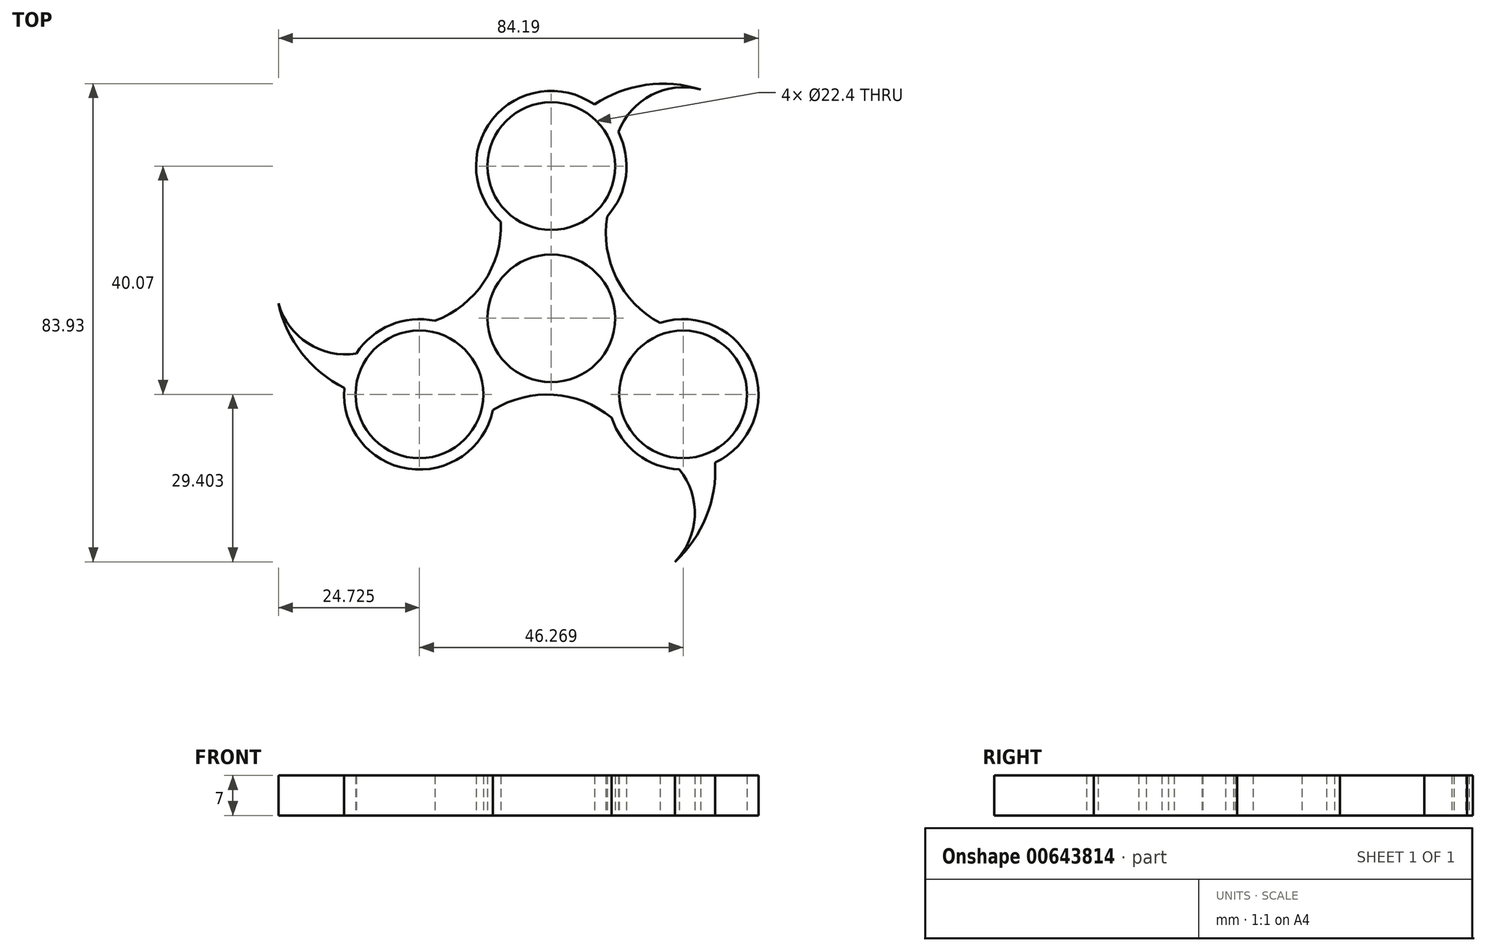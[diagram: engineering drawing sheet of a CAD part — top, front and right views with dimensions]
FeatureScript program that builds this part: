
annotation { "Feature Type Name" : "Feature", "Feature Type Description" : "" }
export const myFeature = defineFeature(function(context is Context, id is Id, definition is map)
    precondition{}
    {
        {
            var Q0;
            Q0=qCreatedBy(makeId("Top.planeOp"),FACE);
            var sketch = newSketch(context, id + "F0", { "sketchPlane" : qUnion([Q0])});
            skCircle(sketch, "E0", {"center": v(0, 0) * mm, "radius": 11.2 * mm});
            skCircle(sketch, "E1", {"center": v(0, 26.71) * mm, "radius": 11.2 * mm});
            skArc(sketch, "E2", {"start": v(9.82, 17.89) * mm, "mid": v(-0.69, 39.9) * mm, "end": v(-8.84, 16.91) * mm});
            skArc(sketch, "E3", {"start": v(26.2, 40.14) * mm, "mid": v(16.58, 40.96) * mm, "end": v(7.57, 37.53) * mm});
            skArc(sketch, "E4", {"start": v(26.2, 40.14) * mm, "mid": v(17.56, 39.18) * mm, "end": v(11.76, 32.7) * mm});
            skArc(sketch, "E5.1.0", {"start": v(-20.4, -0.44) * mm, "mid": v(-34.2, -20.55) * mm, "end": v(-10.23, -16.11) * mm});
            skCircle(sketch, "E5.1.1", {"center": v(-23.13, -13.36) * mm, "radius": 11.2 * mm});
            skArc(sketch, "E5.1.2", {"start": v(-47.86, 2.62) * mm, "mid": v(-43.76, -6.12) * mm, "end": v(-36.28, -12.21) * mm});
            skArc(sketch, "E5.1.3", {"start": v(-47.86, 2.62) * mm, "mid": v(-42.71, -4.39) * mm, "end": v(-34.2, -6.17) * mm});
            skArc(sketch, "E5.2.0", {"start": v(10.58, -17.44) * mm, "mid": v(34.9, -19.35) * mm, "end": v(19.07, -0.8) * mm});
            skCircle(sketch, "E5.2.1", {"center": v(23.13, -13.36) * mm, "radius": 11.2 * mm});
            skArc(sketch, "E5.2.2", {"start": v(21.67, -42.76) * mm, "mid": v(27.18, -34.84) * mm, "end": v(28.72, -25.32) * mm});
            skArc(sketch, "E5.2.3", {"start": v(21.67, -42.76) * mm, "mid": v(25.15, -34.8) * mm, "end": v(22.44, -26.54) * mm});
            skArc(sketch, "E6", {"start": v(9.82, 17.89) * mm, "mid": v(11.43, 7.05) * mm, "end": v(19.07, -0.8) * mm});
            skArc(sketch, "E7.1.1", {"start": v(-20.4, -0.44) * mm, "mid": v(-11.82, 6.37) * mm, "end": v(-8.84, 16.91) * mm});
            skArc(sketch, "E7.2.1", {"start": v(10.58, -17.44) * mm, "mid": v(0.4, -13.42) * mm, "end": v(-10.23, -16.11) * mm});
            skSolve(sketch);
        }
        {
            var Q0;
            Q0 = qSketchRegion(id + "F0", true);
            extrude(context, id + "F1", {"entities" : qUnion([Q0]), "depth" : 7 * mm, "offsetDistance" : 25 * mm});
        }
    });
